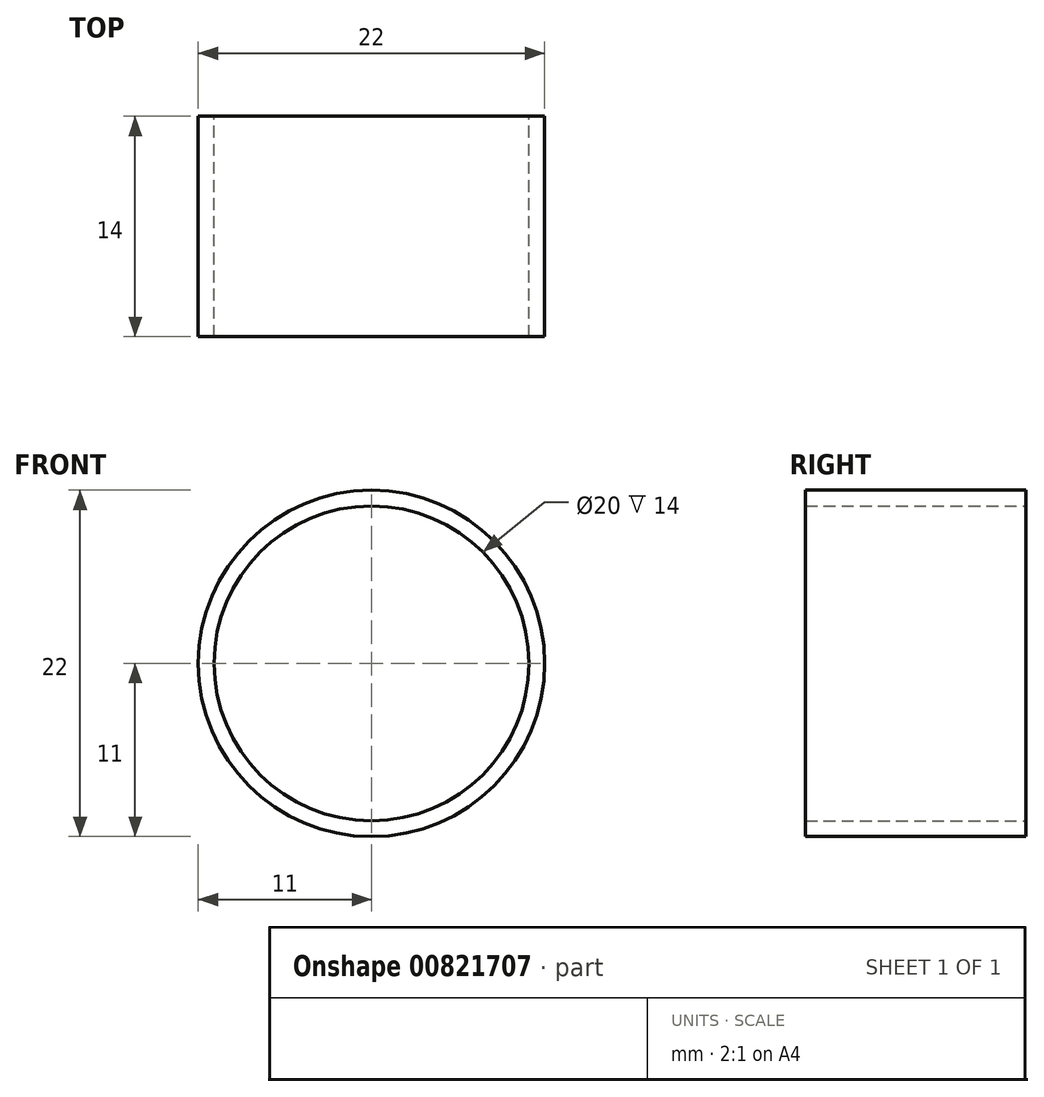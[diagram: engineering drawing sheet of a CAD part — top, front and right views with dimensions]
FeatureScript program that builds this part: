
annotation { "Feature Type Name" : "Feature", "Feature Type Description" : "" }
export const myFeature = defineFeature(function(context is Context, id is Id, definition is map)
    precondition{}
    {
        {
            var Q0;
            Q0=qCreatedBy(makeId("Front.planeOp"),FACE);
            var sketch = newSketch(context, id + "F0", { "sketchPlane" : qUnion([Q0])});
            skCircle(sketch, "E0", {"center": v(0, 0) * mm, "radius": 10 * mm});
            skCircle(sketch, "E1", {"center": v(0, 0) * mm, "radius": 11 * mm});
            skSolve(sketch);
        }
        {
            var Q0;
            Q0 = qSketchRegion(id + "F0", true);
            extrude(context, id + "F1", {"entities" : qUnion([Q0]), "depth" : 14 * mm, "offsetDistance" : 25 * mm});
        }
    });
